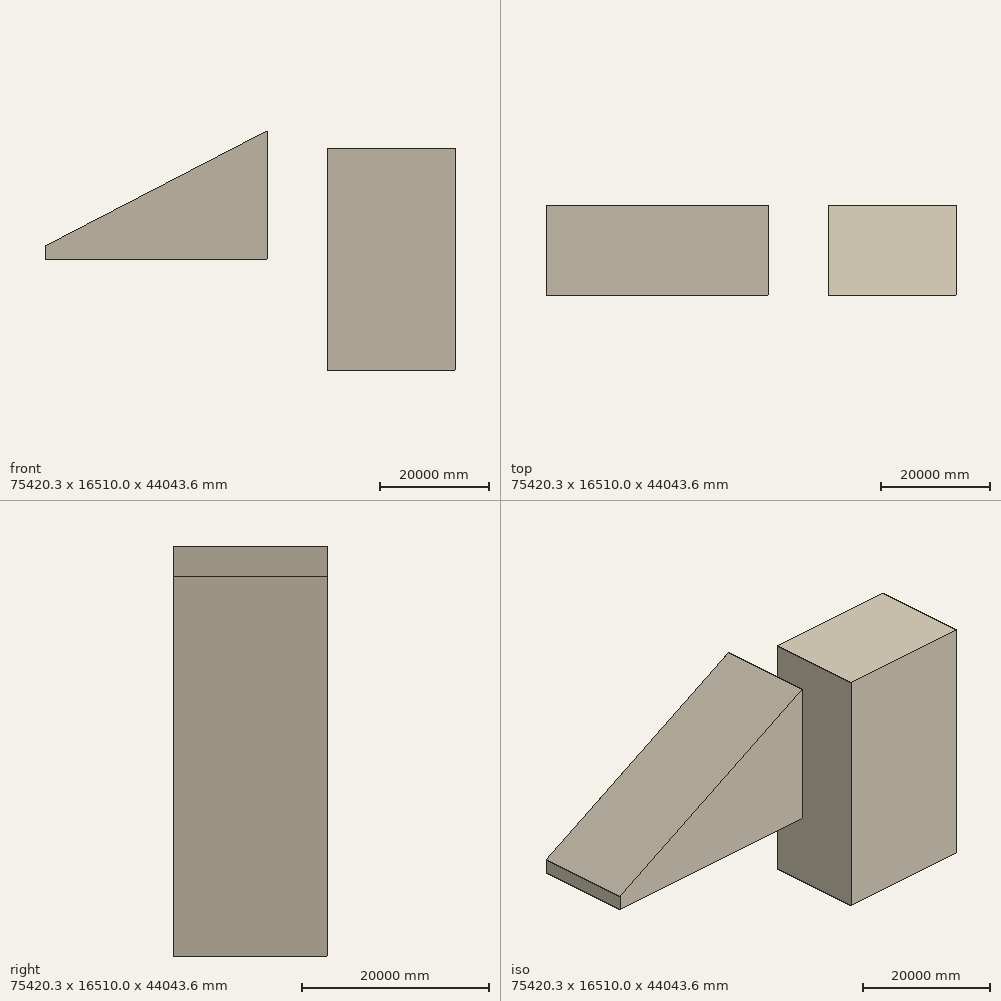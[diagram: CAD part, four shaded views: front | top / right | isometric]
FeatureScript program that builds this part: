
annotation { "Feature Type Name" : "Feature", "Feature Type Description" : "" }
export const myFeature = defineFeature(function(context is Context, id is Id, definition is map)
    precondition{}
    {
        {
            var Q0;
            Q0=qCreatedBy(makeId("Front.planeOp"),FACE);
            var sketch = newSketch(context, id + "F0", { "sketchPlane" : qUnion([Q0])});
            skLineSegment(sketch, "E0.bottom", {"start": v(-11811, -20421.6) * mm, "end": v(11811, -20421.6) * mm});
            skLineSegment(sketch, "E0.top", {"start": v(-11811, 20421.6) * mm, "end": v(11811, 20421.6) * mm});
            skLineSegment(sketch, "E0.left", {"start": v(-11811, -20421.6) * mm, "end": v(-11811, 20421.6) * mm});
            skLineSegment(sketch, "E0.right", {"start": v(11811, -20421.6) * mm, "end": v(11811, 20421.6) * mm});
            skPoint(sketch, "E0.middle", {"position": v(0, 0) * mm});
            skLineSegment(sketch, "E1", {"start": v(-63609.28, 0) * mm, "end": v(-22766.08, 0) * mm});
            skLineSegment(sketch, "E2", {"start": v(-22766.08, 0) * mm, "end": v(-22766.08, 23622) * mm});
            skLineSegment(sketch, "E3", {"start": v(-22766.08, 23622) * mm, "end": v(-63609.28, 2413) * mm});
            skLineSegment(sketch, "E4", {"start": v(-63609.28, 2413) * mm, "end": v(-63609.28, 0) * mm});
            skLineSegment(sketch, "E5", {"start": v(-62403.9, 0) * mm, "end": v(-62403.9, 2413) * mm});
            skLineSegment(sketch, "E6", {"start": v(-25621.58, 0) * mm, "end": v(-25621.58, 22139.2) * mm});
            skSolve(sketch);
        }
        {
            var Q0;
            Q0 = qSketchRegion(id + "F0", true);
            extrude(context, id + "F1", {"entities" : qUnion([Q0]), "depth" : 16510 * mm, "offsetDistance" : 25.4 * mm});
        }
    });
